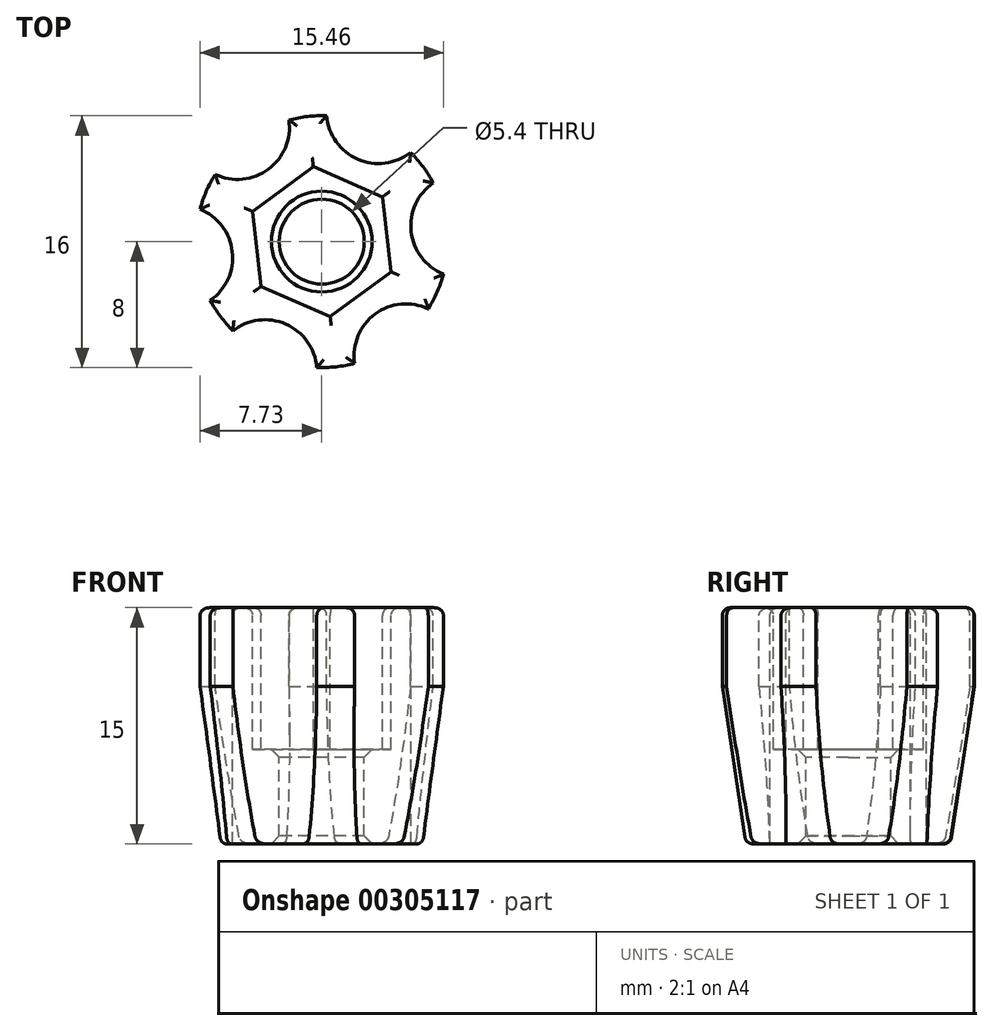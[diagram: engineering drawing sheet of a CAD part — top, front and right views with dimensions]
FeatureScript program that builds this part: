
annotation { "Feature Type Name" : "Feature", "Feature Type Description" : "" }
export const myFeature = defineFeature(function(context is Context, id is Id, definition is map)
    precondition{}
    {
        {
            var Q0;
            Q0=qCreatedBy(makeId("Top.planeOp"),FACE);
            var sketch = newSketch(context, id + "F0", { "sketchPlane" : qUnion([Q0])});
            skCircle(sketch, "E0", {"center": v(0, 0) * mm, "radius": 2.1 * mm});
            skCircle(sketch, "E1", {"center": v(0, 0) * mm, "radius": 6 * mm});
            skSolve(sketch);
        }
        {
            var Q0;
            Q0=makeQuery(id+"F0.imprint","IMPRINT",FACE,{"disambiguationData":[TD([[makeQuery(id+"F0.imprint","IMPRINT",EDGE,{"derivedFrom":sQuery(id+"F0.wireOp",EDGE,"E0")}),-1.0]])]});
            extrude(context, id + "F1", {"entities" : qUnion([Q0]), "depth" : 10 * mm});
        }
        {
            var Q0;
            Q0=qCreatedBy(makeId("Front.planeOp"),FACE);
            var sketch = newSketch(context, id + "F2", { "sketchPlane" : qUnion([Q0])});
            skLineSegment(sketch, "E2", {"start": v(0, 10) * mm, "end": v(0, 20) * mm});
            skLineSegment(sketch, "E3", {"start": v(0, 20) * mm, "end": v(8, 20) * mm});
            skLineSegment(sketch, "E4", {"start": v(8, 20) * mm, "end": v(0, 10) * mm});
            skLineSegment(sketch, "E5", {"start": v(0, 10) * mm, "end": v(6.5, 10) * mm});
            skLineSegment(sketch, "E6", {"start": v(6.5, 10) * mm, "end": v(8, 20) * mm});
            skLineSegment(sketch, "E7", {"start": v(0, 20) * mm, "end": v(2.1, 20) * mm});
            skLineSegment(sketch, "E8", {"start": v(2.1, 20) * mm, "end": v(2.1, 10) * mm});
            skSolve(sketch);
        }
        {
            var Q0;
            {var subQ0=sQuery(id+"F2.wireOp",EDGE,"E3");Q0=makeQuery(id+"F2.imprint","IMPRINT",FACE,{"disambiguationData":[TD([[makeQuery(id+"F2.imprint","IMPRINT",EDGE,{"derivedFrom":subQ0}),-1.0]])]});}
            var Q1;
            {var subQ0=sQuery(id+"F2.wireOp",EDGE,"E6");Q1=makeQuery(id+"F2.imprint","IMPRINT",FACE,{"disambiguationData":[TD([[makeQuery(id+"F2.imprint","IMPRINT",EDGE,{"derivedFrom":subQ0}),1.0]])]});}
            var Q2;
            Q2=sQuery(id+"F2.wireOp",EDGE,"E2");
            revolve(context, id + "F3", {"operationType" : NewBodyOperationType.ADD, "entities" : qUnion([Q0, Q1]), "axis" : qUnion([Q2]), "revolveType" : RevolveType.FULL});
        }
        {
            var Q0;
            Q0=makeQuery(id+"F3.opRevolve","SWEPT_FACE",FACE,{"disambiguationData":[OSD([sQuery(id+"F2.wireOp",EDGE,"E3")])]});
            var sketch = newSketch(context, id + "F4", { "sketchPlane" : qUnion([Q0])});
            skCircle(sketch, "E9.cCircle", {"center": v(0, 0) * mm, "radius": 5.25 * mm, "construction": true});
            skLineSegment(sketch, "E9.0", {"start": v(5.56, -2.42) * mm, "end": v(0.68, -6.02) * mm});
            skLineSegment(sketch, "E9.1", {"start": v(0.68, -6.02) * mm, "end": v(-4.88, -3.6) * mm});
            skLineSegment(sketch, "E9.2", {"start": v(-4.88, -3.6) * mm, "end": v(-5.56, 2.42) * mm});
            skLineSegment(sketch, "E9.3", {"start": v(-5.56, 2.42) * mm, "end": v(-0.68, 6.02) * mm});
            skLineSegment(sketch, "E9.4", {"start": v(-0.68, 6.02) * mm, "end": v(4.88, 3.6) * mm});
            skLineSegment(sketch, "E9.5", {"start": v(4.88, 3.6) * mm, "end": v(5.56, -2.42) * mm});
            skPoint(sketch, "E9.0.midPoint", {"position": v(3.12, -4.22) * mm});
            skCircle(sketch, "E10.cCircle", {"center": v(0, 0) * mm, "radius": 3.6 * mm, "construction": true});
            skLineSegment(sketch, "E10.0", {"start": v(-3.81, 1.66) * mm, "end": v(-0.47, 4.13) * mm});
            skLineSegment(sketch, "E10.1", {"start": v(-0.47, 4.13) * mm, "end": v(3.34, 2.47) * mm});
            skLineSegment(sketch, "E10.2", {"start": v(3.34, 2.47) * mm, "end": v(3.81, -1.66) * mm});
            skLineSegment(sketch, "E10.3", {"start": v(3.81, -1.66) * mm, "end": v(0.47, -4.13) * mm});
            skLineSegment(sketch, "E10.4", {"start": v(0.47, -4.13) * mm, "end": v(-3.34, -2.47) * mm});
            skLineSegment(sketch, "E10.5", {"start": v(-3.34, -2.47) * mm, "end": v(-3.81, 1.66) * mm});
            skPoint(sketch, "E10.0.midPoint", {"position": v(-2.14, 2.9) * mm});
            skSolve(sketch);
        }
        {
            var Q0;
            Q0=makeQuery(id+"F4.imprint","IMPRINT",FACE,{"disambiguationData":[TD([[makeQuery(id+"F4.imprint","IMPRINT",EDGE,{"derivedFrom":sQuery(id+"F4.wireOp",EDGE,"E9.0")}),1.0]])]});
            var Q1;
            Q1=makeQuery(id+"F4.imprint","IMPRINT",FACE,{"disambiguationData":[TD([[makeQuery(id+"F4.imprint","IMPRINT",EDGE,{"derivedFrom":sQuery(id+"F4.wireOp",EDGE,"E9.0")}),-1.0]])]});
            extrude(context, id + "F5", {"entities" : qUnion([Q0, Q1]), "operationType" : NewBodyOperationType.ADD, "depth" : 15 * mm});
        }
        {
            var Q0;
            Q0=makeQuery(id+"F5.opExtrude","CAP_FACE",FACE,{"disambiguationData":[OSD([sQuery(id+"F2.wireOp",EDGE,"E3"),sQuery(id+"F2.wireOp",EDGE,"E4"),sQuery(id+"F2.wireOp",EDGE,"E6"),sQuery(id+"F4.wireOp",EDGE,"E9.0"),sQuery(id+"F4.wireOp",EDGE,"E9.1"),sQuery(id+"F4.wireOp",EDGE,"E9.2"),sQuery(id+"F4.wireOp",EDGE,"E9.3"),sQuery(id+"F4.wireOp",EDGE,"E9.4"),sQuery(id+"F4.wireOp",EDGE,"E9.5")])],"isStart":false});
            var sketch = newSketch(context, id + "F6", { "sketchPlane" : qUnion([Q0])});
            skArc(sketch, "E11", {"start": v(1.44, 3.3) * mm, "mid": v(-0.92, 8.13) * mm, "end": v(-2.14, 2.9) * mm});
            skArc(sketch, "E12", {"start": v(-2.14, 2.9) * mm, "mid": v(-7.5, 3.27) * mm, "end": v(-3.58, -0.4) * mm});
            skArc(sketch, "E13", {"start": v(-6.77, 4.27) * mm, "mid": v(-3.4, 4.6) * mm, "end": v(-2.09, 7.72) * mm});
            skArc(sketch, "E14", {"start": v(-1.44, -3.3) * mm, "mid": v(0.92, -8.13) * mm, "end": v(2.14, -2.9) * mm});
            skArc(sketch, "E15", {"start": v(-3.58, -0.4) * mm, "mid": v(-6.58, -4.86) * mm, "end": v(-1.44, -3.3) * mm});
            skArc(sketch, "E16", {"start": v(2.14, -2.9) * mm, "mid": v(7.5, -3.27) * mm, "end": v(3.58, 0.4) * mm});
            skArc(sketch, "E17", {"start": v(3.58, 0.4) * mm, "mid": v(6.58, 4.86) * mm, "end": v(1.44, 3.3) * mm});
            skArc(sketch, "E18", {"start": v(0.32, 8) * mm, "mid": v(2.29, 5.24) * mm, "end": v(5.64, 5.67) * mm});
            skArc(sketch, "E19", {"start": v(7.08, 3.72) * mm, "mid": v(5.68, 0.64) * mm, "end": v(7.73, -2.05) * mm});
            skArc(sketch, "E20", {"start": v(6.77, -4.27) * mm, "mid": v(3.4, -4.6) * mm, "end": v(2.09, -7.72) * mm});
            skArc(sketch, "E21", {"start": v(-0.32, -8) * mm, "mid": v(-2.29, -5.24) * mm, "end": v(-5.64, -5.67) * mm});
            skArc(sketch, "E22", {"start": v(-7.08, -3.72) * mm, "mid": v(-5.68, -0.64) * mm, "end": v(-7.73, 2.05) * mm});
            skSolve(sketch);
        }
        {
            var Q0;
            {var subQ0=sQuery(id+"F6.wireOp",EDGE,"E13");var subQ1=sQuery(id+"F6.wireOp",EDGE,"E11");var subQ4=makeQuery(id+"F6.imprint","INTERSECT",VERTEX,{"derivedFrom":[subQ1,subQ0]});Q0=makeQuery(id+"F6.imprint","IMPRINT",FACE,{"disambiguationData":[TD([[makeQuery(id+"F6.imprint","IMPRINT",EDGE,{"disambiguationData":[TD([[subQ4,1.0]])],"derivedFrom":subQ0}),1.0]])]});}
            var Q1;
            {var subQ0=sQuery(id+"F6.wireOp",EDGE,"E13");var subQ1=sQuery(id+"F6.wireOp",EDGE,"E12");var subQ3=makeQuery(id+"F6.imprint","INTERSECT",VERTEX,{"derivedFrom":[subQ1,subQ0]});Q1=makeQuery(id+"F6.imprint","IMPRINT",FACE,{"disambiguationData":[TD([[makeQuery(id+"F6.imprint","IMPRINT",EDGE,{"disambiguationData":[TD([[subQ3,-1.0]])],"derivedFrom":subQ1}),1.0]])]});}
            var Q2;
            {var subQ0=sQuery(id+"F6.wireOp",EDGE,"E13");var subQ1=sQuery(id+"F6.wireOp",EDGE,"E11");var subQ3=makeQuery(id+"F6.imprint","INTERSECT",VERTEX,{"derivedFrom":[subQ1,subQ0]});Q2=makeQuery(id+"F6.imprint","IMPRINT",FACE,{"disambiguationData":[TD([[makeQuery(id+"F6.imprint","IMPRINT",EDGE,{"disambiguationData":[TD([[subQ3,1.0]])],"derivedFrom":subQ1}),1.0]])]});}
            var Q3;
            {var subQ0=sQuery(id+"F6.wireOp",EDGE,"E22");var subQ1=sQuery(id+"F6.wireOp",EDGE,"E12");var subQ4=makeQuery(id+"F6.imprint","INTERSECT",VERTEX,{"derivedFrom":[subQ1,subQ0]});Q3=makeQuery(id+"F6.imprint","IMPRINT",FACE,{"disambiguationData":[TD([[makeQuery(id+"F6.imprint","IMPRINT",EDGE,{"disambiguationData":[TD([[subQ4,1.0]])],"derivedFrom":subQ0}),1.0]])]});}
            var Q4;
            {var subQ0=sQuery(id+"F6.wireOp",EDGE,"E22");var subQ1=sQuery(id+"F6.wireOp",EDGE,"E12");var subQ3=makeQuery(id+"F6.imprint","INTERSECT",VERTEX,{"derivedFrom":[subQ1,subQ0]});Q4=makeQuery(id+"F6.imprint","IMPRINT",FACE,{"disambiguationData":[TD([[makeQuery(id+"F6.imprint","IMPRINT",EDGE,{"disambiguationData":[TD([[subQ3,1.0]])],"derivedFrom":subQ1}),1.0]])]});}
            var Q5;
            {var subQ0=sQuery(id+"F6.wireOp",EDGE,"E22");var subQ1=sQuery(id+"F6.wireOp",EDGE,"E15");var subQ3=makeQuery(id+"F6.imprint","INTERSECT",VERTEX,{"derivedFrom":[subQ1,subQ0]});Q5=makeQuery(id+"F6.imprint","IMPRINT",FACE,{"disambiguationData":[TD([[makeQuery(id+"F6.imprint","IMPRINT",EDGE,{"disambiguationData":[TD([[subQ3,-1.0]])],"derivedFrom":subQ1}),1.0]])]});}
            var Q6;
            {var subQ0=sQuery(id+"F6.wireOp",EDGE,"E21");var subQ1=sQuery(id+"F6.wireOp",EDGE,"E14");var subQ4=makeQuery(id+"F6.imprint","INTERSECT",VERTEX,{"derivedFrom":[subQ1,subQ0]});Q6=makeQuery(id+"F6.imprint","IMPRINT",FACE,{"disambiguationData":[TD([[makeQuery(id+"F6.imprint","IMPRINT",EDGE,{"disambiguationData":[TD([[subQ4,-1.0]])],"derivedFrom":subQ0}),1.0]])]});}
            var Q7;
            {var subQ0=sQuery(id+"F6.wireOp",EDGE,"E21");var subQ1=sQuery(id+"F6.wireOp",EDGE,"E15");var subQ3=makeQuery(id+"F6.imprint","INTERSECT",VERTEX,{"derivedFrom":[subQ1,subQ0]});Q7=makeQuery(id+"F6.imprint","IMPRINT",FACE,{"disambiguationData":[TD([[makeQuery(id+"F6.imprint","IMPRINT",EDGE,{"disambiguationData":[TD([[subQ3,1.0]])],"derivedFrom":subQ1}),1.0]])]});}
            var Q8;
            {var subQ0=sQuery(id+"F6.wireOp",EDGE,"E21");var subQ1=sQuery(id+"F6.wireOp",EDGE,"E14");var subQ3=makeQuery(id+"F6.imprint","INTERSECT",VERTEX,{"derivedFrom":[subQ1,subQ0]});Q8=makeQuery(id+"F6.imprint","IMPRINT",FACE,{"disambiguationData":[TD([[makeQuery(id+"F6.imprint","IMPRINT",EDGE,{"disambiguationData":[TD([[subQ3,-1.0]])],"derivedFrom":subQ1}),1.0]])]});}
            var Q9;
            {var subQ0=sQuery(id+"F6.wireOp",EDGE,"E20");var subQ1=sQuery(id+"F6.wireOp",EDGE,"E14");var subQ4=makeQuery(id+"F6.imprint","INTERSECT",VERTEX,{"derivedFrom":[subQ1,subQ0]});Q9=makeQuery(id+"F6.imprint","IMPRINT",FACE,{"disambiguationData":[TD([[makeQuery(id+"F6.imprint","IMPRINT",EDGE,{"disambiguationData":[TD([[subQ4,1.0]])],"derivedFrom":subQ0}),1.0]])]});}
            var Q10;
            {var subQ0=sQuery(id+"F6.wireOp",EDGE,"E20");var subQ1=sQuery(id+"F6.wireOp",EDGE,"E16");var subQ3=makeQuery(id+"F6.imprint","INTERSECT",VERTEX,{"derivedFrom":[subQ1,subQ0]});Q10=makeQuery(id+"F6.imprint","IMPRINT",FACE,{"disambiguationData":[TD([[makeQuery(id+"F6.imprint","IMPRINT",EDGE,{"disambiguationData":[TD([[subQ3,-1.0]])],"derivedFrom":subQ1}),1.0]])]});}
            var Q11;
            {var subQ0=sQuery(id+"F6.wireOp",EDGE,"E20");var subQ1=sQuery(id+"F6.wireOp",EDGE,"E14");var subQ3=makeQuery(id+"F6.imprint","INTERSECT",VERTEX,{"derivedFrom":[subQ1,subQ0]});Q11=makeQuery(id+"F6.imprint","IMPRINT",FACE,{"disambiguationData":[TD([[makeQuery(id+"F6.imprint","IMPRINT",EDGE,{"disambiguationData":[TD([[subQ3,1.0]])],"derivedFrom":subQ1}),1.0]])]});}
            var Q12;
            {var subQ0=sQuery(id+"F6.wireOp",EDGE,"E19");var subQ1=sQuery(id+"F6.wireOp",EDGE,"E16");var subQ4=makeQuery(id+"F6.imprint","INTERSECT",VERTEX,{"derivedFrom":[subQ1,subQ0]});Q12=makeQuery(id+"F6.imprint","IMPRINT",FACE,{"disambiguationData":[TD([[makeQuery(id+"F6.imprint","IMPRINT",EDGE,{"disambiguationData":[TD([[subQ4,1.0]])],"derivedFrom":subQ0}),1.0]])]});}
            var Q13;
            {var subQ0=sQuery(id+"F6.wireOp",EDGE,"E19");var subQ1=sQuery(id+"F6.wireOp",EDGE,"E16");var subQ3=makeQuery(id+"F6.imprint","INTERSECT",VERTEX,{"derivedFrom":[subQ1,subQ0]});Q13=makeQuery(id+"F6.imprint","IMPRINT",FACE,{"disambiguationData":[TD([[makeQuery(id+"F6.imprint","IMPRINT",EDGE,{"disambiguationData":[TD([[subQ3,1.0]])],"derivedFrom":subQ1}),1.0]])]});}
            var Q14;
            {var subQ0=sQuery(id+"F6.wireOp",EDGE,"E19");var subQ1=sQuery(id+"F6.wireOp",EDGE,"E17");var subQ3=makeQuery(id+"F6.imprint","INTERSECT",VERTEX,{"derivedFrom":[subQ1,subQ0]});Q14=makeQuery(id+"F6.imprint","IMPRINT",FACE,{"disambiguationData":[TD([[makeQuery(id+"F6.imprint","IMPRINT",EDGE,{"disambiguationData":[TD([[subQ3,-1.0]])],"derivedFrom":subQ1}),1.0]])]});}
            var Q15;
            {var subQ0=sQuery(id+"F6.wireOp",EDGE,"E18");var subQ1=sQuery(id+"F6.wireOp",EDGE,"E11");var subQ4=makeQuery(id+"F6.imprint","INTERSECT",VERTEX,{"derivedFrom":[subQ1,subQ0]});Q15=makeQuery(id+"F6.imprint","IMPRINT",FACE,{"disambiguationData":[TD([[makeQuery(id+"F6.imprint","IMPRINT",EDGE,{"disambiguationData":[TD([[subQ4,-1.0]])],"derivedFrom":subQ0}),1.0]])]});}
            var Q16;
            {var subQ0=sQuery(id+"F6.wireOp",EDGE,"E18");var subQ1=sQuery(id+"F6.wireOp",EDGE,"E11");var subQ3=makeQuery(id+"F6.imprint","INTERSECT",VERTEX,{"derivedFrom":[subQ1,subQ0]});Q16=makeQuery(id+"F6.imprint","IMPRINT",FACE,{"disambiguationData":[TD([[makeQuery(id+"F6.imprint","IMPRINT",EDGE,{"disambiguationData":[TD([[subQ3,-1.0]])],"derivedFrom":subQ1}),1.0]])]});}
            var Q17;
            {var subQ0=sQuery(id+"F6.wireOp",EDGE,"E18");var subQ1=sQuery(id+"F6.wireOp",EDGE,"E17");var subQ3=makeQuery(id+"F6.imprint","INTERSECT",VERTEX,{"derivedFrom":[subQ1,subQ0]});Q17=makeQuery(id+"F6.imprint","IMPRINT",FACE,{"disambiguationData":[TD([[makeQuery(id+"F6.imprint","IMPRINT",EDGE,{"disambiguationData":[TD([[subQ3,1.0]])],"derivedFrom":subQ1}),1.0]])]});}
            extrude(context, id + "F7", {"entities" : qUnion([Q0, Q1, Q2, Q3, Q4, Q5, Q6, Q7, Q8, Q9, Q10, Q11, Q12, Q13, Q14, Q15, Q16, Q17]), "operationType" : NewBodyOperationType.REMOVE, "oppositeDirection" : true, "depth" : 25 * mm});
        }
        {
            var Q0;
            Q0=makeQuery(id+"F5.opExtrude","CAP_FACE",FACE,{"disambiguationData":[OSD([sQuery(id+"F2.wireOp",EDGE,"E3"),sQuery(id+"F2.wireOp",EDGE,"E4"),sQuery(id+"F2.wireOp",EDGE,"E6"),sQuery(id+"F4.wireOp",EDGE,"E9.0"),sQuery(id+"F4.wireOp",EDGE,"E9.1"),sQuery(id+"F4.wireOp",EDGE,"E9.2"),sQuery(id+"F4.wireOp",EDGE,"E9.3"),sQuery(id+"F4.wireOp",EDGE,"E9.4"),sQuery(id+"F4.wireOp",EDGE,"E9.5")])],"isStart":false});
            extrude(context, id + "F8", {"entities" : qUnion([Q0]), "operationType" : NewBodyOperationType.REMOVE, "oppositeDirection" : true, "depth" : 5 * mm});
        }
        {
            var Q0;
            Q0=makeQuery(id+"F1.opExtrude","CAP_FACE",FACE,{"disambiguationData":[OSD([sQuery(id+"F0.wireOp",EDGE,"E0"),sQuery(id+"F0.wireOp",EDGE,"E1")])],"isStart":true});
            extrude(context, id + "F9", {"entities" : qUnion([Q0]), "operationType" : NewBodyOperationType.REMOVE, "oppositeDirection" : true, "depth" : 10 * mm});
        }
        {
            var Q0;
            Q0=makeQuery(id+"F8.boolean.opBoolean","COPY",FACE,{"derivedFrom":makeQuery(id+"F8.opExtrude","CAP_FACE",FACE,{"disambiguationData":[OSD([sQuery(id+"F2.wireOp",EDGE,"E3"),sQuery(id+"F2.wireOp",EDGE,"E4"),sQuery(id+"F2.wireOp",EDGE,"E6"),sQuery(id+"F4.wireOp",EDGE,"E10.0"),sQuery(id+"F4.wireOp",EDGE,"E10.1"),sQuery(id+"F4.wireOp",EDGE,"E10.2"),sQuery(id+"F4.wireOp",EDGE,"E10.3"),sQuery(id+"F4.wireOp",EDGE,"E10.4"),sQuery(id+"F4.wireOp",EDGE,"E10.5")])],"isStart":false})});
            extrude(context, id + "F10", {"entities" : qUnion([Q0]), "operationType" : NewBodyOperationType.REMOVE, "oppositeDirection" : true, "depth" : 5 * mm});
        }
        {
            var Q0;
            Q0=makeQuery(id+"F3.boolean.opBoolean","MERGE",FACE,{"derivedFrom":[makeQuery(id+"F1.opExtrude","SWEPT_FACE",FACE,{"disambiguationData":[OSD([sQuery(id+"F0.wireOp",EDGE,"E0")])]}),makeQuery(id+"F3.opRevolve","SWEPT_FACE",FACE,{"disambiguationData":[OSD([sQuery(id+"F2.wireOp",EDGE,"E8")])]})]});
            chamfer(context, id + "F11", {"entities" : qUnion([Q0]), "width" : 0.5 * mm, "tangentPropagation" : true});
        }
        {
            var Q0;
            {var subQ0=sQuery(id+"F2.wireOp",EDGE,"E5");var subQ1=sQuery(id+"F2.wireOp",EDGE,"E6");Q0=makeQuery(id+"F7.boolean.opBoolean","SPLIT",EDGE,{"disambiguationData":[TD([makeQuery(id+"F3.opRevolve","SWEPT_FACE",FACE,{"disambiguationData":[OSD([subQ0])]}),makeQuery(id+"F3.opRevolve","SWEPT_FACE",FACE,{"disambiguationData":[OSD([subQ1])]}),makeQuery(id+"F7.opExtrude","SWEPT_FACE",FACE,{"disambiguationData":[OSD([sQuery(id+"F6.wireOp",EDGE,"E13")])]}),makeQuery(id+"F7.opExtrude","SWEPT_FACE",FACE,{"disambiguationData":[OSD([sQuery(id+"F6.wireOp",EDGE,"E18")])]})])],"derivedFrom":makeQuery(id+"F3.opRevolve","SWEPT_EDGE",EDGE,{"disambiguationData":[OSD([subQ0,subQ1])]})});}
            var Q1;
            {var subQ0=sQuery(id+"F2.wireOp",EDGE,"E5");var subQ1=sQuery(id+"F2.wireOp",EDGE,"E6");Q1=makeQuery(id+"F7.boolean.opBoolean","SPLIT",EDGE,{"disambiguationData":[TD([makeQuery(id+"F3.opRevolve","SWEPT_FACE",FACE,{"disambiguationData":[OSD([subQ0])]}),makeQuery(id+"F3.opRevolve","SWEPT_FACE",FACE,{"disambiguationData":[OSD([subQ1])]}),makeQuery(id+"F7.opExtrude","SWEPT_FACE",FACE,{"disambiguationData":[OSD([sQuery(id+"F6.wireOp",EDGE,"E18")])]}),makeQuery(id+"F7.opExtrude","SWEPT_FACE",FACE,{"disambiguationData":[OSD([sQuery(id+"F6.wireOp",EDGE,"E19")])]})])],"derivedFrom":makeQuery(id+"F3.opRevolve","SWEPT_EDGE",EDGE,{"disambiguationData":[OSD([subQ0,subQ1])]})});}
            var Q2;
            {var subQ0=sQuery(id+"F2.wireOp",EDGE,"E5");var subQ1=sQuery(id+"F2.wireOp",EDGE,"E6");Q2=makeQuery(id+"F7.boolean.opBoolean","SPLIT",EDGE,{"disambiguationData":[TD([makeQuery(id+"F3.opRevolve","SWEPT_FACE",FACE,{"disambiguationData":[OSD([subQ0])]}),makeQuery(id+"F3.opRevolve","SWEPT_FACE",FACE,{"disambiguationData":[OSD([subQ1])]}),makeQuery(id+"F7.opExtrude","SWEPT_FACE",FACE,{"disambiguationData":[OSD([sQuery(id+"F6.wireOp",EDGE,"E13")])]}),makeQuery(id+"F7.opExtrude","SWEPT_FACE",FACE,{"disambiguationData":[OSD([sQuery(id+"F6.wireOp",EDGE,"E22")])]})])],"derivedFrom":makeQuery(id+"F3.opRevolve","SWEPT_EDGE",EDGE,{"disambiguationData":[OSD([subQ0,subQ1])]})});}
            var Q3;
            {var subQ0=sQuery(id+"F2.wireOp",EDGE,"E5");var subQ1=sQuery(id+"F2.wireOp",EDGE,"E6");Q3=makeQuery(id+"F7.boolean.opBoolean","SPLIT",EDGE,{"disambiguationData":[TD([makeQuery(id+"F3.opRevolve","SWEPT_FACE",FACE,{"disambiguationData":[OSD([subQ0])]}),makeQuery(id+"F3.opRevolve","SWEPT_FACE",FACE,{"disambiguationData":[OSD([subQ1])]}),makeQuery(id+"F7.opExtrude","SWEPT_FACE",FACE,{"disambiguationData":[OSD([sQuery(id+"F6.wireOp",EDGE,"E21")])]}),makeQuery(id+"F7.opExtrude","SWEPT_FACE",FACE,{"disambiguationData":[OSD([sQuery(id+"F6.wireOp",EDGE,"E22")])]})])],"derivedFrom":makeQuery(id+"F3.opRevolve","SWEPT_EDGE",EDGE,{"disambiguationData":[OSD([subQ0,subQ1])]})});}
            var Q4;
            {var subQ0=sQuery(id+"F2.wireOp",EDGE,"E5");var subQ1=sQuery(id+"F2.wireOp",EDGE,"E6");Q4=makeQuery(id+"F7.boolean.opBoolean","SPLIT",EDGE,{"disambiguationData":[TD([makeQuery(id+"F3.opRevolve","SWEPT_FACE",FACE,{"disambiguationData":[OSD([subQ0])]}),makeQuery(id+"F3.opRevolve","SWEPT_FACE",FACE,{"disambiguationData":[OSD([subQ1])]}),makeQuery(id+"F7.opExtrude","SWEPT_FACE",FACE,{"disambiguationData":[OSD([sQuery(id+"F6.wireOp",EDGE,"E20")])]}),makeQuery(id+"F7.opExtrude","SWEPT_FACE",FACE,{"disambiguationData":[OSD([sQuery(id+"F6.wireOp",EDGE,"E21")])]})])],"derivedFrom":makeQuery(id+"F3.opRevolve","SWEPT_EDGE",EDGE,{"disambiguationData":[OSD([subQ0,subQ1])]})});}
            var Q5;
            {var subQ0=sQuery(id+"F2.wireOp",EDGE,"E5");var subQ1=sQuery(id+"F2.wireOp",EDGE,"E6");Q5=makeQuery(id+"F7.boolean.opBoolean","SPLIT",EDGE,{"disambiguationData":[TD([makeQuery(id+"F3.opRevolve","SWEPT_FACE",FACE,{"disambiguationData":[OSD([subQ0])]}),makeQuery(id+"F3.opRevolve","SWEPT_FACE",FACE,{"disambiguationData":[OSD([subQ1])]}),makeQuery(id+"F7.opExtrude","SWEPT_FACE",FACE,{"disambiguationData":[OSD([sQuery(id+"F6.wireOp",EDGE,"E19")])]}),makeQuery(id+"F7.opExtrude","SWEPT_FACE",FACE,{"disambiguationData":[OSD([sQuery(id+"F6.wireOp",EDGE,"E20")])]})])],"derivedFrom":makeQuery(id+"F3.opRevolve","SWEPT_EDGE",EDGE,{"disambiguationData":[OSD([subQ0,subQ1])]})});}
            var Q6;
            {var subQ0=sQuery(id+"F6.wireOp",EDGE,"E22");Q6=makeQuery(id+"F7.boolean.opBoolean","COPY",EDGE,{"disambiguationData":[topologyDisambiguationEdgeConnected([makeQuery(id+"F7.opExtrude","SWEPT_FACE",FACE,{"disambiguationData":[OSD([subQ0])]}),makeQuery(id+"F7.opExtrude","CAP_FACE",FACE,{"disambiguationData":[OSD([sQuery(id+"F2.wireOp",EDGE,"E3"),sQuery(id+"F2.wireOp",EDGE,"E4"),sQuery(id+"F2.wireOp",EDGE,"E6"),subQ0])],"isStart":false})])],"derivedFrom":makeQuery(id+"F7.opExtrude","CAP_EDGE",EDGE,{"disambiguationData":[OSD([subQ0])],"isStart":false})});}
            var Q7;
            {var subQ0=sQuery(id+"F6.wireOp",EDGE,"E21");Q7=makeQuery(id+"F7.boolean.opBoolean","COPY",EDGE,{"disambiguationData":[topologyDisambiguationEdgeConnected([makeQuery(id+"F7.opExtrude","SWEPT_FACE",FACE,{"disambiguationData":[OSD([subQ0])]}),makeQuery(id+"F7.opExtrude","CAP_FACE",FACE,{"disambiguationData":[OSD([sQuery(id+"F2.wireOp",EDGE,"E3"),sQuery(id+"F2.wireOp",EDGE,"E4"),sQuery(id+"F2.wireOp",EDGE,"E6"),subQ0])],"isStart":false})])],"derivedFrom":makeQuery(id+"F7.opExtrude","CAP_EDGE",EDGE,{"disambiguationData":[OSD([subQ0])],"isStart":false})});}
            var Q8;
            {var subQ0=sQuery(id+"F6.wireOp",EDGE,"E20");Q8=makeQuery(id+"F7.boolean.opBoolean","COPY",EDGE,{"disambiguationData":[topologyDisambiguationEdgeConnected([makeQuery(id+"F7.opExtrude","SWEPT_FACE",FACE,{"disambiguationData":[OSD([subQ0])]}),makeQuery(id+"F7.opExtrude","CAP_FACE",FACE,{"disambiguationData":[OSD([sQuery(id+"F2.wireOp",EDGE,"E3"),sQuery(id+"F2.wireOp",EDGE,"E4"),sQuery(id+"F2.wireOp",EDGE,"E6"),subQ0])],"isStart":false})])],"derivedFrom":makeQuery(id+"F7.opExtrude","CAP_EDGE",EDGE,{"disambiguationData":[OSD([subQ0])],"isStart":false})});}
            var Q9;
            {var subQ0=sQuery(id+"F6.wireOp",EDGE,"E19");Q9=makeQuery(id+"F7.boolean.opBoolean","COPY",EDGE,{"disambiguationData":[topologyDisambiguationEdgeConnected([makeQuery(id+"F7.opExtrude","SWEPT_FACE",FACE,{"disambiguationData":[OSD([subQ0])]}),makeQuery(id+"F7.opExtrude","CAP_FACE",FACE,{"disambiguationData":[OSD([sQuery(id+"F2.wireOp",EDGE,"E3"),sQuery(id+"F2.wireOp",EDGE,"E4"),sQuery(id+"F2.wireOp",EDGE,"E6"),subQ0])],"isStart":false})])],"derivedFrom":makeQuery(id+"F7.opExtrude","CAP_EDGE",EDGE,{"disambiguationData":[OSD([subQ0])],"isStart":false})});}
            var Q10;
            {var subQ0=sQuery(id+"F6.wireOp",EDGE,"E18");Q10=makeQuery(id+"F7.boolean.opBoolean","COPY",EDGE,{"disambiguationData":[topologyDisambiguationEdgeConnected([makeQuery(id+"F7.opExtrude","SWEPT_FACE",FACE,{"disambiguationData":[OSD([subQ0])]}),makeQuery(id+"F7.opExtrude","CAP_FACE",FACE,{"disambiguationData":[OSD([sQuery(id+"F2.wireOp",EDGE,"E3"),sQuery(id+"F2.wireOp",EDGE,"E4"),sQuery(id+"F2.wireOp",EDGE,"E6"),subQ0])],"isStart":false})])],"derivedFrom":makeQuery(id+"F7.opExtrude","CAP_EDGE",EDGE,{"disambiguationData":[OSD([subQ0])],"isStart":false})});}
            var Q11;
            {var subQ0=sQuery(id+"F6.wireOp",EDGE,"E13");Q11=makeQuery(id+"F7.boolean.opBoolean","COPY",EDGE,{"disambiguationData":[topologyDisambiguationEdgeConnected([makeQuery(id+"F7.opExtrude","SWEPT_FACE",FACE,{"disambiguationData":[OSD([subQ0])]}),makeQuery(id+"F7.opExtrude","CAP_FACE",FACE,{"disambiguationData":[OSD([sQuery(id+"F2.wireOp",EDGE,"E3"),sQuery(id+"F2.wireOp",EDGE,"E4"),sQuery(id+"F2.wireOp",EDGE,"E6"),subQ0])],"isStart":false})])],"derivedFrom":makeQuery(id+"F7.opExtrude","CAP_EDGE",EDGE,{"disambiguationData":[OSD([subQ0])],"isStart":false})});}
            fillet(context, id + "F12", {"entities" : qUnion([Q0, Q1, Q2, Q3, Q4, Q5, Q6, Q7, Q8, Q9, Q10, Q11]), "radius" : 0.5 * mm, "tangentPropagation" : true, "allowEdgeOverflow" : false});
        }
        {
            var Q0;
            Q0=makeQuery(id+"F3.opRevolve","SWEPT_FACE",FACE,{"disambiguationData":[OSD([sQuery(id+"F2.wireOp",EDGE,"E3")])]});
            extrude(context, id + "F13", {"entities" : qUnion([Q0]), "operationType" : NewBodyOperationType.REMOVE, "oppositeDirection" : true, "depth" : 4 * mm});
        }
        {
            var Q0;
            Q0=makeQuery(id+"F10.boolean.opBoolean","COPY",FACE,{"derivedFrom":makeQuery(id+"F10.opExtrude","CAP_FACE",FACE,{"disambiguationData":[OSD([sQuery(id+"F2.wireOp",EDGE,"E3"),sQuery(id+"F2.wireOp",EDGE,"E4"),sQuery(id+"F2.wireOp",EDGE,"E6"),sQuery(id+"F4.wireOp",EDGE,"E10.0"),sQuery(id+"F4.wireOp",EDGE,"E10.1"),sQuery(id+"F4.wireOp",EDGE,"E10.2"),sQuery(id+"F4.wireOp",EDGE,"E10.3"),sQuery(id+"F4.wireOp",EDGE,"E10.4"),sQuery(id+"F4.wireOp",EDGE,"E10.5")])],"isStart":false})});
            var sketch = newSketch(context, id + "F14", { "sketchPlane" : qUnion([Q0])});
            skCircle(sketch, "E23", {"center": v(0, 0) * mm, "radius": 2.7 * mm});
            skCircle(sketch, "E24.cCircle", {"center": v(0, 0) * mm, "radius": 4.15 * mm, "construction": true});
            skLineSegment(sketch, "E24.0", {"start": v(-0.54, 4.76) * mm, "end": v(3.86, 2.85) * mm});
            skLineSegment(sketch, "E24.1", {"start": v(3.86, 2.85) * mm, "end": v(4.4, -1.92) * mm});
            skLineSegment(sketch, "E24.2", {"start": v(4.4, -1.92) * mm, "end": v(0.54, -4.76) * mm});
            skLineSegment(sketch, "E24.3", {"start": v(0.54, -4.76) * mm, "end": v(-3.86, -2.85) * mm});
            skLineSegment(sketch, "E24.4", {"start": v(-3.86, -2.85) * mm, "end": v(-4.4, 1.92) * mm});
            skLineSegment(sketch, "E24.5", {"start": v(-4.4, 1.92) * mm, "end": v(-0.54, 4.76) * mm});
            skPoint(sketch, "E24.0.midPoint", {"position": v(1.66, 3.8) * mm});
            skSolve(sketch);
        }
        {
            var Q0;
            Q0=makeQuery(id+"F14.imprint","IMPRINT",FACE,{"disambiguationData":[TD([[makeQuery(id+"F14.imprint","IMPRINT",EDGE,{"derivedFrom":sQuery(id+"F14.wireOp",EDGE,"E23")}),1.0]])]});
            extrude(context, id + "F15", {"entities" : qUnion([Q0]), "operationType" : NewBodyOperationType.REMOVE, "endBound" : BoundingType.THROUGH_ALL, "oppositeDirection" : true, "depth" : 25 * mm});
        }
        {
            var Q0;
            Q0=makeQuery(id+"F14.imprint","IMPRINT",FACE,{"disambiguationData":[TD([[makeQuery(id+"F14.imprint","IMPRINT",EDGE,{"derivedFrom":sQuery(id+"F14.wireOp",EDGE,"E24.0")}),-1.0]])]});
            extrude(context, id + "F16", {"entities" : qUnion([Q0]), "operationType" : NewBodyOperationType.REMOVE, "oppositeDirection" : true, "depth" : 9 * mm});
        }
        {
            var Q0;
            Q0=makeQuery(id+"F15.boolean.opBoolean","COPY",FACE,{"derivedFrom":makeQuery(id+"F15.opExtrude","SWEPT_FACE",FACE,{"disambiguationData":[OSD([sQuery(id+"F14.wireOp",EDGE,"E23")])]})});
            chamfer(context, id + "F17", {"entities" : qUnion([Q0]), "width" : 0.5 * mm, "tangentPropagation" : true});
        }
        {
            var Q0;
            Q0=makeQuery(id+"F10.boolean.opBoolean","COPY",FACE,{"derivedFrom":makeQuery(id+"F10.opExtrude","CAP_FACE",FACE,{"disambiguationData":[OSD([sQuery(id+"F2.wireOp",EDGE,"E3"),sQuery(id+"F2.wireOp",EDGE,"E4"),sQuery(id+"F2.wireOp",EDGE,"E6"),sQuery(id+"F4.wireOp",EDGE,"E10.0"),sQuery(id+"F4.wireOp",EDGE,"E10.1"),sQuery(id+"F4.wireOp",EDGE,"E10.2"),sQuery(id+"F4.wireOp",EDGE,"E10.3"),sQuery(id+"F4.wireOp",EDGE,"E10.4"),sQuery(id+"F4.wireOp",EDGE,"E10.5")])],"isStart":false})});
            fillet(context, id + "F18", {"entities" : qUnion([Q0]), "radius" : 0.5 * mm, "tangentPropagation" : true, "allowEdgeOverflow" : false});
        }
    });
